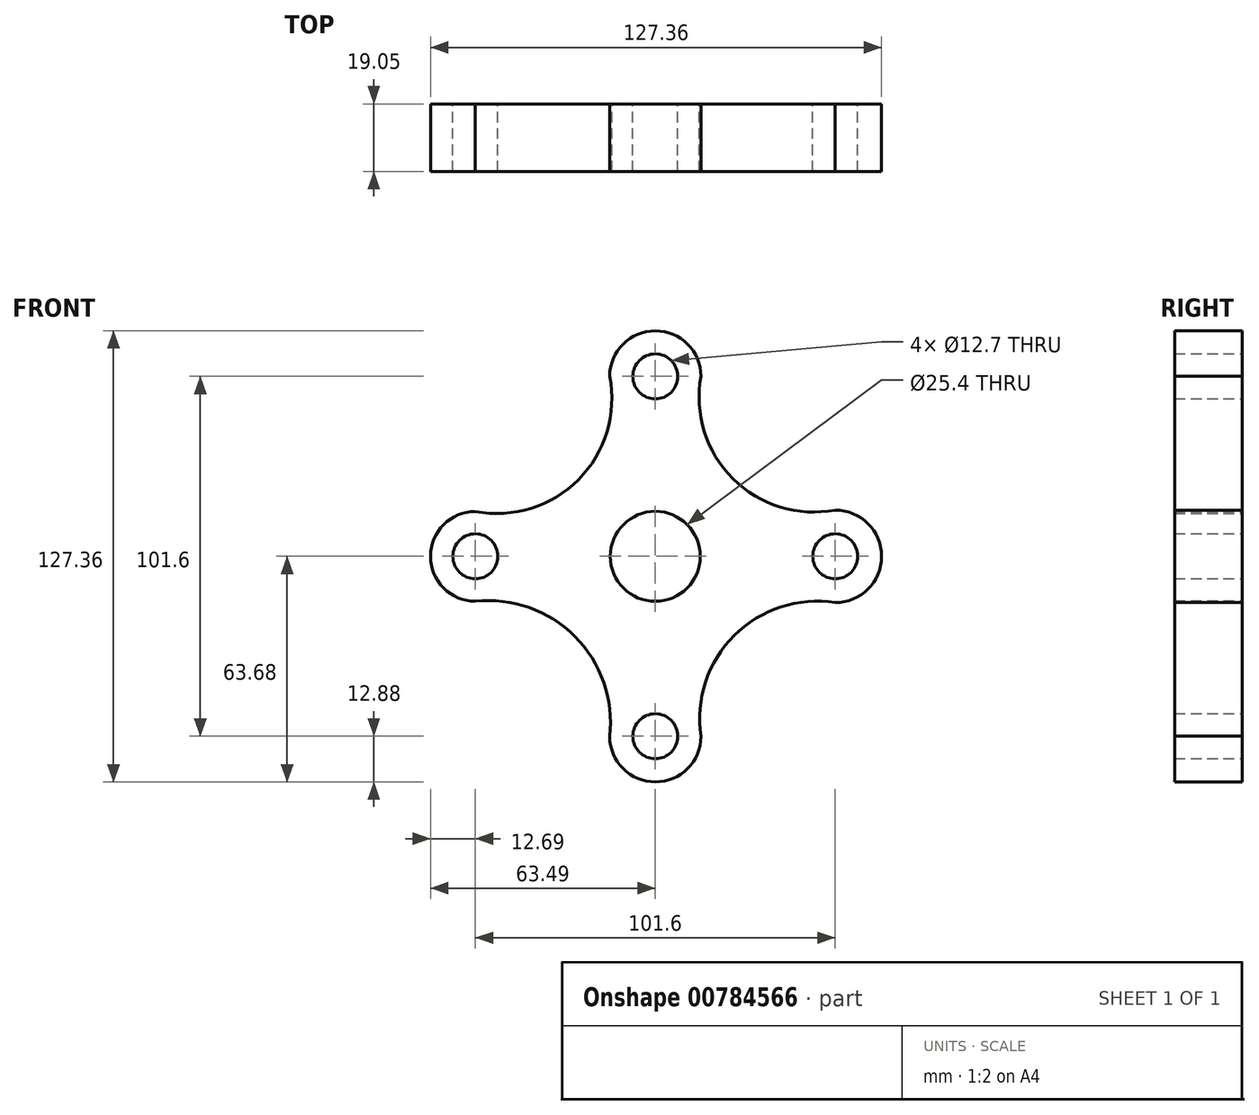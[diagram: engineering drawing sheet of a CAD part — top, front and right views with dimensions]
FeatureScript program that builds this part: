
annotation { "Feature Type Name" : "Feature", "Feature Type Description" : "" }
export const myFeature = defineFeature(function(context is Context, id is Id, definition is map)
    precondition{}
    {
        {
            var Q0;
            Q0=qCreatedBy(makeId("Front.planeOp"),FACE);
            var sketch = newSketch(context, id + "F0", { "sketchPlane" : qUnion([Q0])});
            skCircle(sketch, "E0", {"center": v(0, 0) * mm, "radius": 12.7 * mm});
            skLineSegment(sketch, "E1", {"start": v(0, 0) * mm, "end": v(0, 50.8) * mm});
            skCircle(sketch, "E2", {"center": v(0, 50.8) * mm, "radius": 6.35 * mm});
            skLineSegment(sketch, "E3", {"start": v(0, 0) * mm, "end": v(50.8, 0) * mm});
            skCircle(sketch, "E4", {"center": v(50.8, 0) * mm, "radius": 6.35 * mm});
            skLineSegment(sketch, "E5", {"start": v(0, 0) * mm, "end": v(0, -50.8) * mm});
            skCircle(sketch, "E6", {"center": v(0, -50.8) * mm, "radius": 6.35 * mm});
            skLineSegment(sketch, "E7", {"start": v(0, 0) * mm, "end": v(-50.8, 0) * mm});
            skCircle(sketch, "E8", {"center": v(-50.8, 0) * mm, "radius": 6.35 * mm});
            skArc(sketch, "E9", {"start": v(0, 63.68) * mm, "mid": v(9.1, 59.9) * mm, "end": v(12.88, 50.8) * mm});
            skArc(sketch, "E10", {"start": v(0, 63.68) * mm, "mid": v(-9.1, 59.9) * mm, "end": v(-12.88, 50.8) * mm});
            skArc(sketch, "E11", {"start": v(-63.5, 0) * mm, "mid": v(-59.77, -8.97) * mm, "end": v(-50.8, -12.7) * mm});
            skArc(sketch, "E12", {"start": v(-63.5, 0) * mm, "mid": v(-59.77, 8.97) * mm, "end": v(-50.8, 12.7) * mm});
            skArc(sketch, "E13", {"start": v(63.87, 0) * mm, "mid": v(60.04, -9.24) * mm, "end": v(50.8, -13.07) * mm});
            skArc(sketch, "E14", {"start": v(63.87, 0) * mm, "mid": v(60.04, 9.24) * mm, "end": v(50.8, 13.07) * mm});
            skArc(sketch, "E15", {"start": v(0, -63.68) * mm, "mid": v(9.1, -59.9) * mm, "end": v(12.88, -50.8) * mm});
            skArc(sketch, "E16", {"start": v(0, -63.68) * mm, "mid": v(-9.1, -59.9) * mm, "end": v(-12.88, -50.8) * mm});
            skArc(sketch, "E17", {"start": v(-12.88, -50.8) * mm, "mid": v(-22.66, -22.61) * mm, "end": v(-50.8, -12.7) * mm});
            skArc(sketch, "E18", {"start": v(50.8, -13.07) * mm, "mid": v(22.29, -22.33) * mm, "end": v(12.88, -50.8) * mm});
            skArc(sketch, "E19", {"start": v(12.88, 50.8) * mm, "mid": v(21.9, 21.94) * mm, "end": v(50.8, 13.07) * mm});
            skArc(sketch, "E20", {"start": v(-50.8, 12.7) * mm, "mid": v(-21.7, 21.66) * mm, "end": v(-12.88, 50.8) * mm});
            skSolve(sketch);
        }
        {
            var Q0;
            Q0 = qSketchRegion(id + "F0", true);
            extrude(context, id + "F1", {"entities" : qUnion([Q0]), "depth" : 19.05 * mm, "offsetDistance" : 25.4 * mm});
        }
    });
